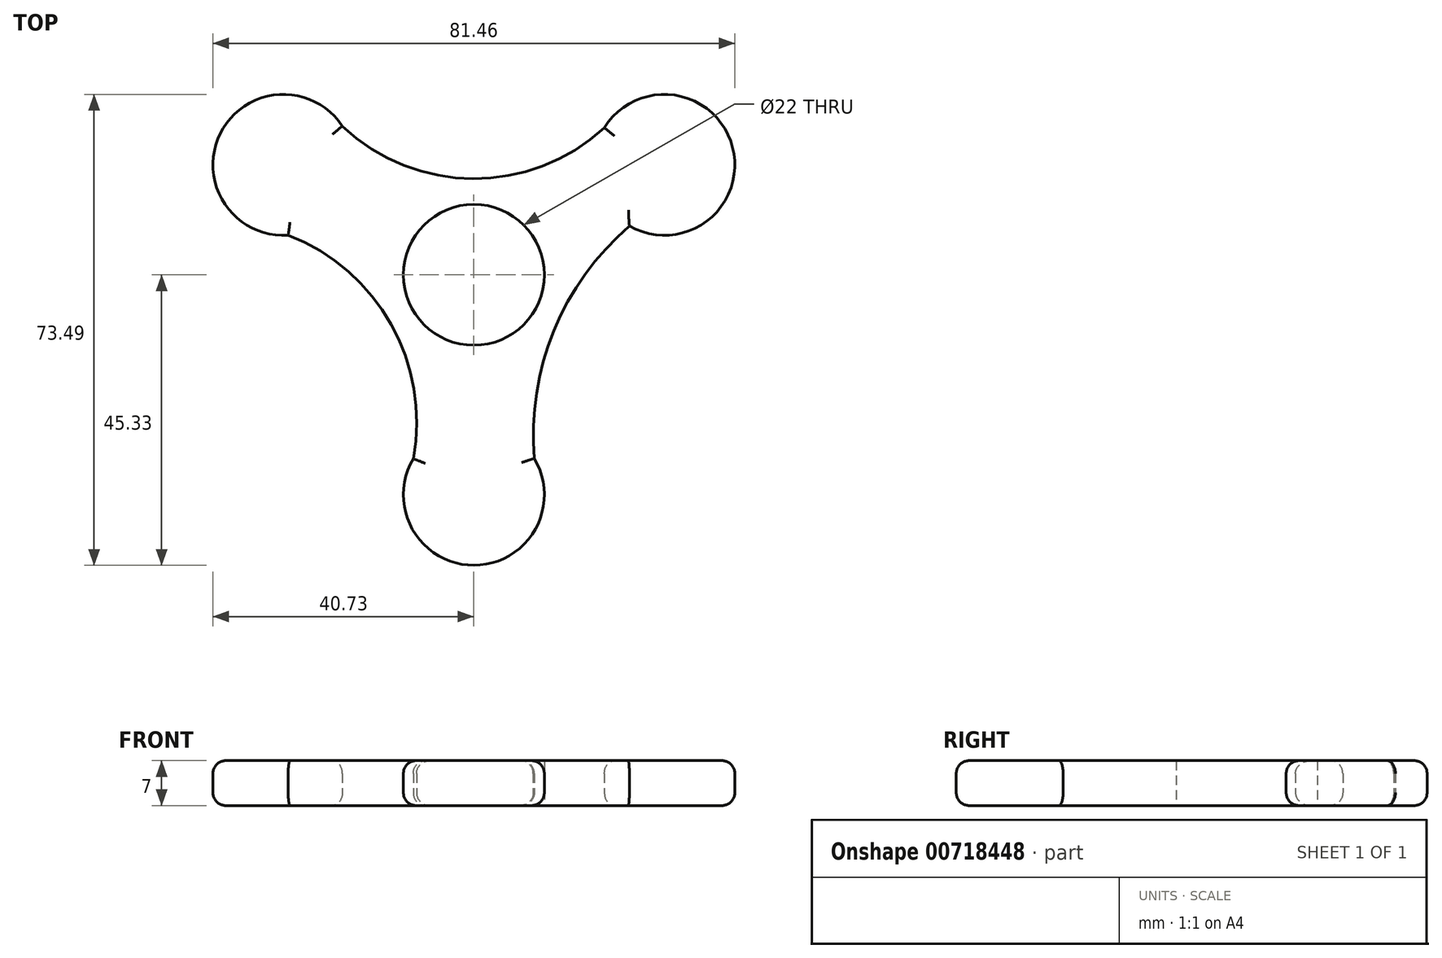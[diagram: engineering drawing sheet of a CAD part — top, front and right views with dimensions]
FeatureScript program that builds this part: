
annotation { "Feature Type Name" : "Feature", "Feature Type Description" : "" }
export const myFeature = defineFeature(function(context is Context, id is Id, definition is map)
    precondition{}
    {
        {
            var Q0;
            Q0=qCreatedBy(makeId("Top.planeOp"),FACE);
            var sketch = newSketch(context, id + "F0", { "sketchPlane" : qUnion([Q0])});
            skCircle(sketch, "E0", {"center": v(0, 0) * mm, "radius": 11 * mm});
            skCircle(sketch, "E1", {"center": v(0, -34.33) * mm, "radius": 11 * mm});
            skCircle(sketch, "E2.1.0", {"center": v(29.73, 17.16) * mm, "radius": 11 * mm});
            skCircle(sketch, "E2.2.0", {"center": v(-29.73, 17.16) * mm, "radius": 11 * mm});
            skArc(sketch, "E3", {"start": v(-20.54, 23.2) * mm, "mid": v(-0.13, 15) * mm, "end": v(20.38, 22.95) * mm});
            skArc(sketch, "E4", {"start": v(-9.45, -28.7) * mm, "mid": v(-12.91, -7.73) * mm, "end": v(-28.98, 6.19) * mm});
            skArc(sketch, "E5", {"start": v(24.28, 7.6) * mm, "mid": v(12.49, -8.74) * mm, "end": v(9.43, -28.66) * mm});
            skSolve(sketch);
        }
        {
            var Q0;
            Q0 = qSketchRegion(id + "F0", true);
            extrude(context, id + "F1", {"entities" : qUnion([Q0]), "depth" : 7 * mm, "offsetDistance" : 25 * mm});
        }
        {
            var Q0;
            Q0=makeQuery(id+"F1.opExtrude","CAP_EDGE",EDGE,{"disambiguationData":[OSD([sQuery(id+"F0.wireOp",EDGE,"E3")])],"isStart":false});
            var Q1;
            Q1=makeQuery(id+"F1.opExtrude","CAP_EDGE",EDGE,{"disambiguationData":[OSD([sQuery(id+"F0.wireOp",EDGE,"E5")])],"isStart":false});
            var Q2;
            Q2=makeQuery(id+"F1.opExtrude","CAP_EDGE",EDGE,{"disambiguationData":[OSD([sQuery(id+"F0.wireOp",EDGE,"E4")])],"isStart":false});
            var Q3;
            Q3=makeQuery(id+"F1.opExtrude","CAP_EDGE",EDGE,{"disambiguationData":[OSD([sQuery(id+"F0.wireOp",EDGE,"E2.2.0")])],"isStart":false});
            var Q4;
            Q4=makeQuery(id+"F1.opExtrude","CAP_EDGE",EDGE,{"disambiguationData":[OSD([sQuery(id+"F0.wireOp",EDGE,"E2.1.0")])],"isStart":false});
            var Q5;
            Q5=makeQuery(id+"F1.opExtrude","CAP_EDGE",EDGE,{"disambiguationData":[OSD([sQuery(id+"F0.wireOp",EDGE,"E1")])],"isStart":false});
            var Q6;
            Q6=makeQuery(id+"F1.opExtrude","CAP_EDGE",EDGE,{"disambiguationData":[OSD([sQuery(id+"F0.wireOp",EDGE,"E4")])],"isStart":true});
            var Q7;
            Q7=makeQuery(id+"F1.opExtrude","CAP_EDGE",EDGE,{"disambiguationData":[OSD([sQuery(id+"F0.wireOp",EDGE,"E2.1.0")])],"isStart":true});
            var Q8;
            Q8=makeQuery(id+"F1.opExtrude","CAP_EDGE",EDGE,{"disambiguationData":[OSD([sQuery(id+"F0.wireOp",EDGE,"E2.2.0")])],"isStart":true});
            var Q9;
            Q9=makeQuery(id+"F1.opExtrude","CAP_EDGE",EDGE,{"disambiguationData":[OSD([sQuery(id+"F0.wireOp",EDGE,"E5")])],"isStart":true});
            var Q10;
            Q10=makeQuery(id+"F1.opExtrude","CAP_EDGE",EDGE,{"disambiguationData":[OSD([sQuery(id+"F0.wireOp",EDGE,"E1")])],"isStart":true});
            var Q11;
            Q11=makeQuery(id+"F1.opExtrude","CAP_EDGE",EDGE,{"disambiguationData":[OSD([sQuery(id+"F0.wireOp",EDGE,"E3")])],"isStart":true});
            fillet(context, id + "F2", {"entities" : qUnion([Q0, Q1, Q2, Q3, Q4, Q5, Q6, Q7, Q8, Q9, Q10, Q11]), "radius" : 2 * mm, "tangentPropagation" : true, "allowEdgeOverflow" : false});
        }
    });
